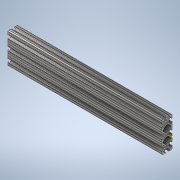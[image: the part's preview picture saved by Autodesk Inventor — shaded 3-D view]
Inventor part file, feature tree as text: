
AUTODESK INVENTOR PART (.ipt)
format: ipt  version: 2020 (Build 240168000, 168)  size: 379,392 bytes
history: native  units: in
note: dims shown in document units (in); Inventor stores cm internally (conversion verified against a paired STEP export)
features: sketch x2, extrude x1
ambient origin geometry x8: Origin, YZ Plane, XZ Plane, XY Plane, X Axis, Y Axis, Z Axis, Center Point
bodies: Solid1 (feature_tree)
feature tree (3):
  extrude  "Extrusion1"  [1 undecoded]
  sketch  "Sketch2"
  sketch  "Sketch1"  dims[d0=15.0in d1=0.0in]
note: 1 required parameter value undecoded (feature->parameter linkage not recoverable at this tier; creation-order binding heuristic only, values carry confidence <= 0.55)
